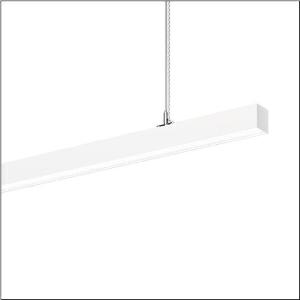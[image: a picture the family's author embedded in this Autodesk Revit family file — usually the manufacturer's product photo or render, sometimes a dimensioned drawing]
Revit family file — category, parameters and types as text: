
# Revit family: silica_r__21_51mx30tbt5w_3ed0
name_source: partatom
category: Lighting Fixtures
units: mm (PartAtom-declared; Revit-internal decimal feet)

## family parameters
Cut with Voids When Loaded = No
Host = Face
Light Source = No
Part Type = Normal
Room Calculation Point = No
Round Connector Dimension = Use Diameter
Shared = No

## types (1)
- --- (1 x LED, 5150 lm, 42.2 W, 6500K)
    Apparent Load = 42 VA
    CIE Flux Codes = 47 79 96 58 100
    Color Rendering = 80
    Color Temperature = 6500K
    Default Elevation = 1800 mm
    Description = Silica® 21, office luminaire, primary optical cover: cover, of PMMA, opal, light emission: direct/indirect distribution, primary light characteristic: symmetric, installation type: suspended mounting, LED, rated luminous flux: 5.150lm, luminous efficacy: 116lm/W, light colour: 8tw, colour temperature: 2700..6500K, control gear: ECG DALI, with terminal, 3+2-pole, max. 2.5mm², mains connection: 220..240V, AC, 50/60Hz, rated input power: 44.3W, luminaire housing, of aluminium, traffic white (RAL 9016), length: 1.504mm, width: 53mm, height: 53mm, protection rating (complete): IP20, insulation class (complete): insulation class I (protective earthing), certification: CE, permissible operating ambient temperature: 0..+35°C, standard: EN 50419, packaging unit: 1 piece
    Height = 53 mm
    Lamp = 1 x LED
    Lamp Light Flux = 5150 lm
    Lamp Power = 42.2 W
    Lamp count = 1
    Length = 1504 mm
    Luminous efficacy = 122 lm/W
    Manufacturer = Siteco
    ModVariant = No
    Model = 51MX30TBT5W
    Mounting Place = Ceiling
    Mounting Type = Pendant
    Number of Poles = 1
    OnlyDefault = Yes
    Power Factor = 1
    Product Name = Silica® 21
    Product group = office luminaire | ceiling pendant
    ProductGroupID = 902
    Protection Class = Protection class I
    Protection Degree = IP 20
    RLX_Detail_Level = 1
    RLX_Emergency_Light_Flux = 0 lm
    RLX_Emergency_Type = 0
    RLX_Emergency_Type_DB = No
    RlxData = <blob elided: 18177 chars, md5=2844de57>
    Socket = socket
    Standby Power = 0 W
    System Light Flux = 5150 lm
    System Power = 42 W
    Type Comments = individual setting
    Type Image = l_1297784.jpg
    URL = http://relux.com
    VarID = @adj_070975
    Voltage = 0 V
    Weight = 0.00 kg
    Width = 53 mm

## geometry (parser evidence)
native form markers: Blend x4, Sweep x11
no freeform markers — native parametric forms only
